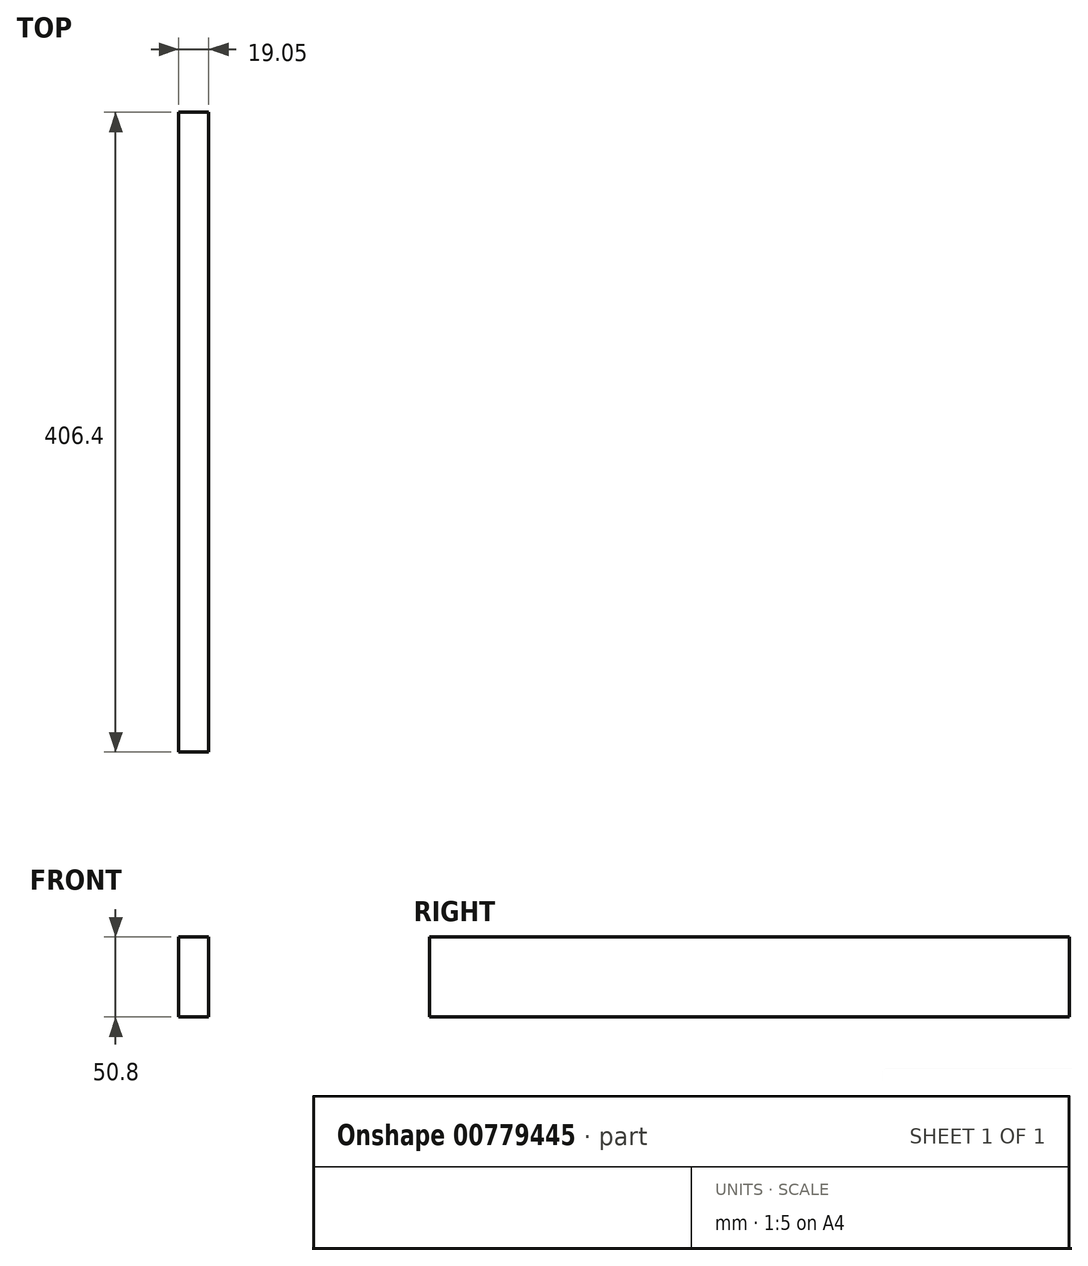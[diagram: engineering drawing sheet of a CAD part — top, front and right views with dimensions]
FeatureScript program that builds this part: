
annotation { "Feature Type Name" : "Feature", "Feature Type Description" : "" }
export const myFeature = defineFeature(function(context is Context, id is Id, definition is map)
    precondition{}
    {
        {
            var Q0;
            Q0=qCreatedBy(makeId("Right.planeOp"),FACE);
            var sketch = newSketch(context, id + "F0", { "sketchPlane" : qUnion([Q0])});
            skLineSegment(sketch, "E0.bottom", {"start": v(-203.2, 25.4) * mm, "end": v(203.2, 25.4) * mm});
            skLineSegment(sketch, "E0.top", {"start": v(-203.2, -25.4) * mm, "end": v(203.2, -25.4) * mm});
            skLineSegment(sketch, "E0.left", {"start": v(-203.2, 25.4) * mm, "end": v(-203.2, -25.4) * mm});
            skLineSegment(sketch, "E0.right", {"start": v(203.2, 25.4) * mm, "end": v(203.2, -25.4) * mm});
            skPoint(sketch, "E0.middle", {"position": v(0, 0) * mm});
            skSolve(sketch);
        }
        {
            var Q0;
            Q0=makeQuery(id+"F0.imprint","IMPRINT",FACE,{"disambiguationData":[TD([[makeQuery(id+"F0.imprint","IMPRINT",EDGE,{"derivedFrom":sQuery(id+"F0.wireOp",EDGE,"E0.bottom")}),-1.0]])]});
            extrude(context, id + "F1", {"entities" : qUnion([Q0]), "depth" : 19.05 * mm, "offsetDistance" : 25.4 * mm});
        }
    });
